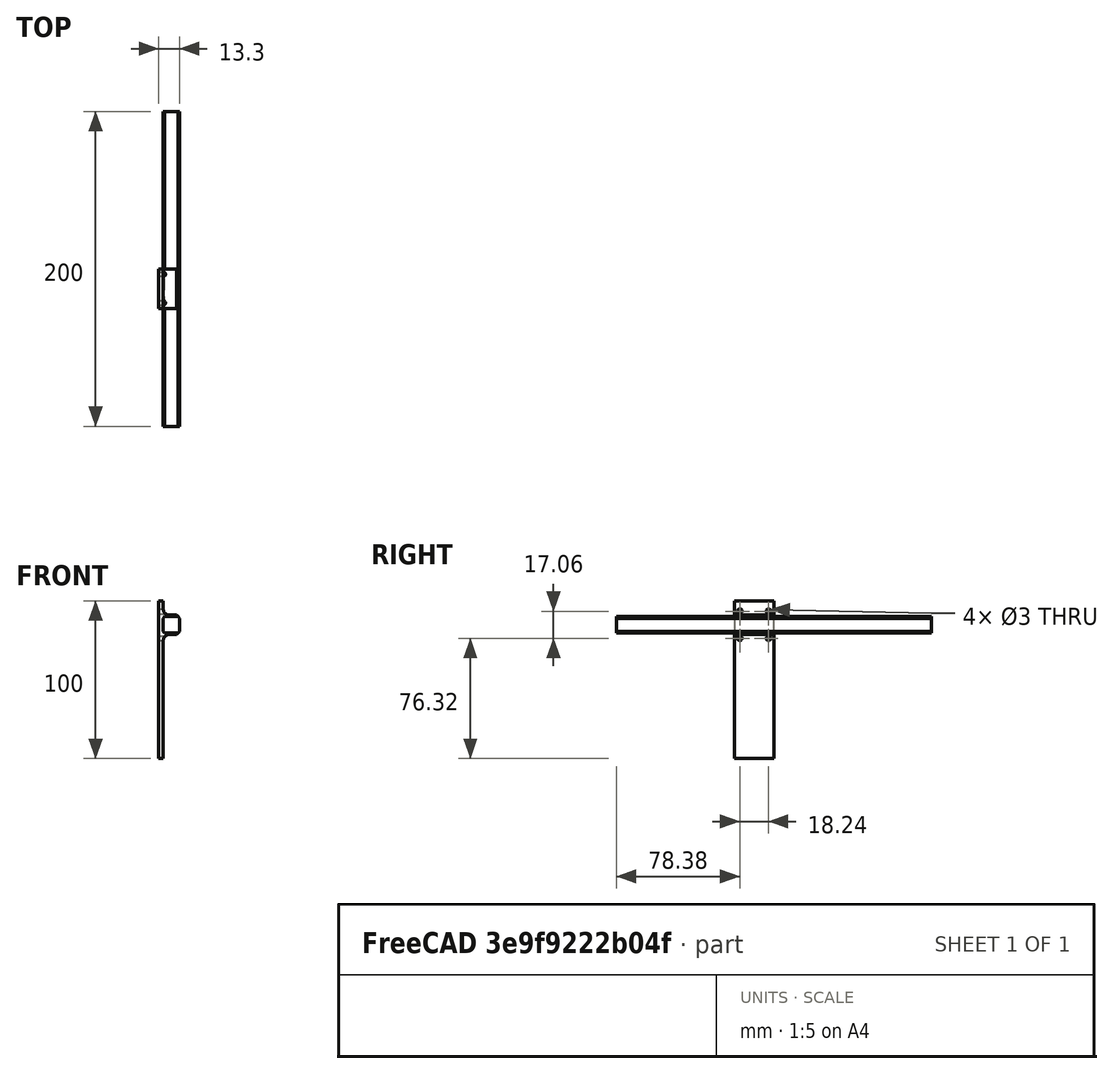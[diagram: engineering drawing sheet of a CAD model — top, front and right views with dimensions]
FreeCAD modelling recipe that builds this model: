
FCSTD DOCUMENT  (FreeCAD 0.18R13728 (Git))
Label: test111_trico_leg
License: All rights reserved
LicenseURL: http://en.wikipedia.org/wiki/All_rights_reserved
objects: Sketcher::SketchObject×4, Part::Extrusion×4, Part::Chamfer×2, Part::MultiFuse×1, Part::Fillet×1, Part::Cut×1, Mesh::Feature×1
note: 13 computed .brp shape members not serialized (recipe doc carries the construction recipe); baked Part::Feature solids carry a one-line shape summary decoded from their .brp

FEATURE [Sketcher::SketchObject] Sketch003
  MapMode = 2
  Placement = pos=(0,0,0) rot=(1,0,0;1.5708rad)
  sketch-geometry (4):
    g0: LineSegment StartX=-5.15 StartY=-5.15 StartZ=0 EndX=5.15 EndY=-5.15 EndZ=0
    g1: LineSegment StartX=5.15 StartY=-5.15 StartZ=0 EndX=5.15 EndY=5.15 EndZ=0
    g2: LineSegment StartX=5.15 StartY=5.15 StartZ=0 EndX=-5.15 EndY=5.15 EndZ=0
    g3: LineSegment StartX=-5.15 StartY=5.15 StartZ=0 EndX=-5.15 EndY=-5.15 EndZ=0
  constraints (11):
    c: Coincident(g0,g1)
    c: Coincident(g1,g2)
    c: Coincident(g2,g3)
    c: Coincident(g3,g0)
    c: Horizontal(g0)
    c: Horizontal(g2)
    c: Vertical(g1)
    c: Vertical(g3)
    c: Symmetric(g3,g1,g-1)
    c: Equal(g1,g0)
    c: Distance(g1) = 10.3
FEATURE [Part::Extrusion] Extrude
  Base = -> Sketch003
  Dir = (0,-1,0)
  DirMode = 2
  FaceMakerClass = Part::FaceMakerBullseye
  LengthFwd = 100
  LengthRev = 100
  Solid = true
  Symmetric = false
FEATURE [Part::Chamfer] Chamfer
  Base = -> Extrude
  Edges = 4 edges r=1: [Edge1,Edge2,Edge5,Edge8]
FEATURE [Sketcher::SketchObject] Sketch
  ExternalGeometry = -> [Chamfer]
  MapMode = 5
  Placement = pos=(-5.15,0,0) rot=(0.57735,-0.57735,-0.57735;2.0944rad)
  Support = -> [Chamfer]
  sketch-geometry (4):
    g0: LineSegment StartX=0 StartY=15.15 StartZ=0 EndX=25 EndY=15.15 EndZ=0
    g1: LineSegment StartX=25 StartY=15.15 StartZ=0 EndX=25 EndY=-84.85 EndZ=0
    g2: LineSegment StartX=25 StartY=-84.85 StartZ=0 EndX=0 EndY=-84.85 EndZ=0
    g3: LineSegment StartX=0 StartY=-84.85 StartZ=0 EndX=0 EndY=15.15 EndZ=0
  constraints (12):
    c: Coincident(g0,g1)
    c: Coincident(g1,g2)
    c: Coincident(g2,g3)
    c: Coincident(g3,g0)
    c: Horizontal(g0)
    c: Horizontal(g2)
    c: Vertical(g1)
    c: Vertical(g3)
    c: PointOnObject(g0,g-2)
    c: Distance(g3) = 100
    c: Distance(g0,g-3) = 10
    c: Distance(g0) = 25
FEATURE [Part::Extrusion] Extrude001
  Base = -> Sketch
  Dir = (-1,0,0)
  DirMode = 2
  FaceMakerClass = Part::FaceMakerBullseye
  LengthFwd = 3
  LengthRev = 0
  Solid = true
  Symmetric = false
FEATURE [Sketcher::SketchObject] Sketch004
  ExternalGeometry = -> [Chamfer,Extrude001]
  MapMode = 5
  Placement = pos=(0,0,0) rot=(0,0.707107,0.707107;3.14159rad)
  Support = -> [Extrude001]
  sketch-geometry (10):
    g0: LineSegment StartX=5.15 StartY=4.15 StartZ=0 EndX=4.15 EndY=5.15 EndZ=0
    g1: LineSegment StartX=4.15 StartY=5.15 StartZ=0 EndX=-4.15 EndY=5.15 EndZ=0
    g2: LineSegment StartX=-4.15 StartY=5.15 StartZ=0 EndX=-4.15 EndY=6.15 EndZ=0
    g3: LineSegment StartX=-4.15 StartY=6.15 StartZ=0 EndX=5.15 EndY=6.15 EndZ=0
    g4: LineSegment StartX=5.15 StartY=4.15 StartZ=0 EndX=5.15 EndY=6.15 EndZ=0
    g5: LineSegment StartX=5.15 StartY=-4.15 StartZ=0 EndX=4.15 EndY=-5.15 EndZ=0
    g6: LineSegment StartX=4.15 StartY=-5.15 StartZ=0 EndX=-4.15 EndY=-5.15 EndZ=0
    g7: LineSegment StartX=-4.15 StartY=-5.15 StartZ=0 EndX=-4.15 EndY=-6.15 EndZ=0
    g8: LineSegment StartX=-4.15 StartY=-6.15 StartZ=0 EndX=5.15 EndY=-6.15 EndZ=0
    g9: LineSegment StartX=5.15 StartY=-4.15 StartZ=0 EndX=5.15 EndY=-6.15 EndZ=0
  constraints (25):
    c: Coincident(g0,g-5)
    c: Coincident(g0,g-6)
    c: Coincident(g1,g0)
    c: Coincident(g1,g-6)
    c: Coincident(g1,g2)
    c: Vertical(g2)
    c: Coincident(g2,g3)
    c: Horizontal(g3)
    c: PointOnObject(g3,g-8)
    c: Distance(g2) = 1
    c: Coincident(g4,g0)
    c: Coincident(g4,g3)
    c: Coincident(g6,g5)
    c: Coincident(g6,g7)
    c: Vertical(g7)
    c: Coincident(g7,g8)
    c: Horizontal(g8)
    c: Coincident(g9,g5)
    c: Coincident(g9,g8)
    c: Symmetric(g1,g6,g-1)
    c: Symmetric(g0,g5,g-1)
    c: PointOnObject(g8,g-8)
    c: Horizontal(g6)
    c: Symmetric(g5,g0,g-1)
    c: Equal(g7,g2)
FEATURE [Part::Extrusion] Extrude002
  Base = -> Sketch004
  Dir = (0,1,0)
  DirMode = 2
  FaceMakerClass = Part::FaceMakerBullseye
  LengthFwd = 0
  LengthRev = 25
  Solid = true
  Symmetric = false
FEATURE [Part::MultiFuse] Fusion
  Shapes = -> [Extrude002,Extrude001]
FEATURE [Part::Fillet] Fillet
  Base = -> Fusion
  Edges = 2 edges r=4: [Edge19,Edge22]
FEATURE [Part::Chamfer] Chamfer001
  Base = -> Fillet
  Edges = 2 edges r=0.9: [Edge42,Edge52]
FEATURE [Sketcher::SketchObject] Sketch005
  ExternalGeometry = -> [Chamfer,Chamfer001]
  MapMode = 5
  Placement = pos=(-8.15,0,0) rot=(0.57735,-0.57735,-0.57735;2.0944rad)
  Support = -> [Chamfer001]
  sketch-geometry (10):
    g0: Circle CenterX=3.38009 CenterY=8.53009 CenterZ=0 NormalX=0 NormalY=0 NormalZ=1 AngleXU=0 Radius=1.5
    g1: GeomPoint X=12.5 Y=0 Z=0
    g2: GeomPoint X=25 Y=0 Z=0
    g3: Circle [constr] CenterX=3.38009 CenterY=8.53009 CenterZ=0 NormalX=0 NormalY=0 NormalZ=1 AngleXU=0 Radius=3.38009
    g4: Circle CenterX=21.6199 CenterY=-8.53009 CenterZ=0 NormalX=0 NormalY=0 NormalZ=1 AngleXU=0 Radius=1.5
    g5: Circle [constr] CenterX=21.6199 CenterY=-8.53009 CenterZ=0 NormalX=0 NormalY=0 NormalZ=1 AngleXU=0 Radius=3.38009
    g6: Circle CenterX=3.38009 CenterY=-8.53009 CenterZ=0 NormalX=0 NormalY=0 NormalZ=1 AngleXU=0 Radius=1.5
    g7: Circle [constr] CenterX=3.38009 CenterY=-8.53009 CenterZ=0 NormalX=0 NormalY=0 NormalZ=1 AngleXU=0 Radius=3.38009
    g8: Circle CenterX=21.6199 CenterY=8.53009 CenterZ=0 NormalX=0 NormalY=0 NormalZ=1 AngleXU=0 Radius=1.5
    g9: Circle [constr] CenterX=21.6199 CenterY=8.53009 CenterZ=0 NormalX=0 NormalY=0 NormalZ=1 AngleXU=0 Radius=3.38009
  constraints (22):
    c: PointOnObject(g2,g-5)
    c: PointOnObject(g2,g-1)
    c: Symmetric(g2,g-1,g1)
    c: Coincident(g3,g0)
    c: Tangent(g3,g-3)
    c: Tangent(g-2,g3)
    c: Radius(g0) = 1.5
    c: Coincident(g5,g4)
    c: Radius(g4) = 1.5
    c: Coincident(g7,g6)
    c: Radius(g6) = 1.5
    c: Coincident(g9,g8)
    c: Radius(g8) = 1.5
    c: Tangent(g9,g-3)
    c: Tangent(g9,g-5)
    c: Tangent(g5,g-5)
    c: Tangent(g5,g-4)
    c: Tangent(g7,g-4)
    c: Tangent(g7,g-2)
    c: Equal(g9,g3)
    c: Equal(g3,g7)
    c: Equal(g3,g5)
FEATURE [Part::Extrusion] Extrude003
  Base = -> Sketch005
  Dir = (-1,0,0)
  DirMode = 2
  FaceMakerClass = Part::FaceMakerBullseye
  LengthFwd = 20
  LengthRev = 20
  Solid = true
  Symmetric = false
FEATURE [Part::Cut] Cut
  Base = -> Chamfer001
  Tool = -> Extrude003
FEATURE [Mesh::Feature] Mesh  label="Cut (Meshed)"
